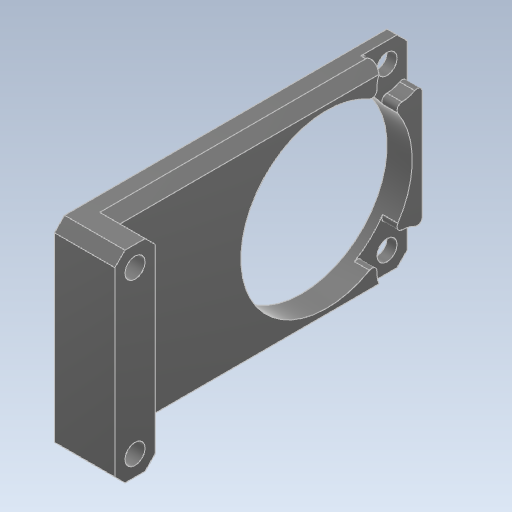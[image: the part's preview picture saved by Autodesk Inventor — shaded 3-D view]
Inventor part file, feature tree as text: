
AUTODESK INVENTOR PART (.ipt)
format: ipt  version: 2024 (Build 280153000, 153)  size: 184,320 bytes
history: native  units: mm
features: other x4, extrude x2, chamfer x2, sketch x1, fillet x1
ambient origin geometry x8: Origin, YZ Plane, XZ Plane, XY Plane, X Axis, Y Axis, Z Axis, Center Point
bodies: Body1 (feature_tree)
feature tree (10):
  other  "_bridseye_sketch.ipt"
  sketch  "スケッチ2"
  extrude  "押し出し1"  Depth=10.0mm
  extrude  "押し出し2"  Depth=5.0mm
  chamfer  "面取り2"  Distance=1.5mm
  chamfer  "面取り1"  [1 undecoded]
  fillet  "フィレット1"  Radius=1.0mm
  other  "ソリッド32::_bridseye_sketch.ipt"
  other  "TaggingFeature1"
  other  "side_links-link2"
note: 1 required parameter value undecoded (feature->parameter linkage not recoverable at this tier; creation-order binding heuristic only, values carry confidence <= 0.55)
